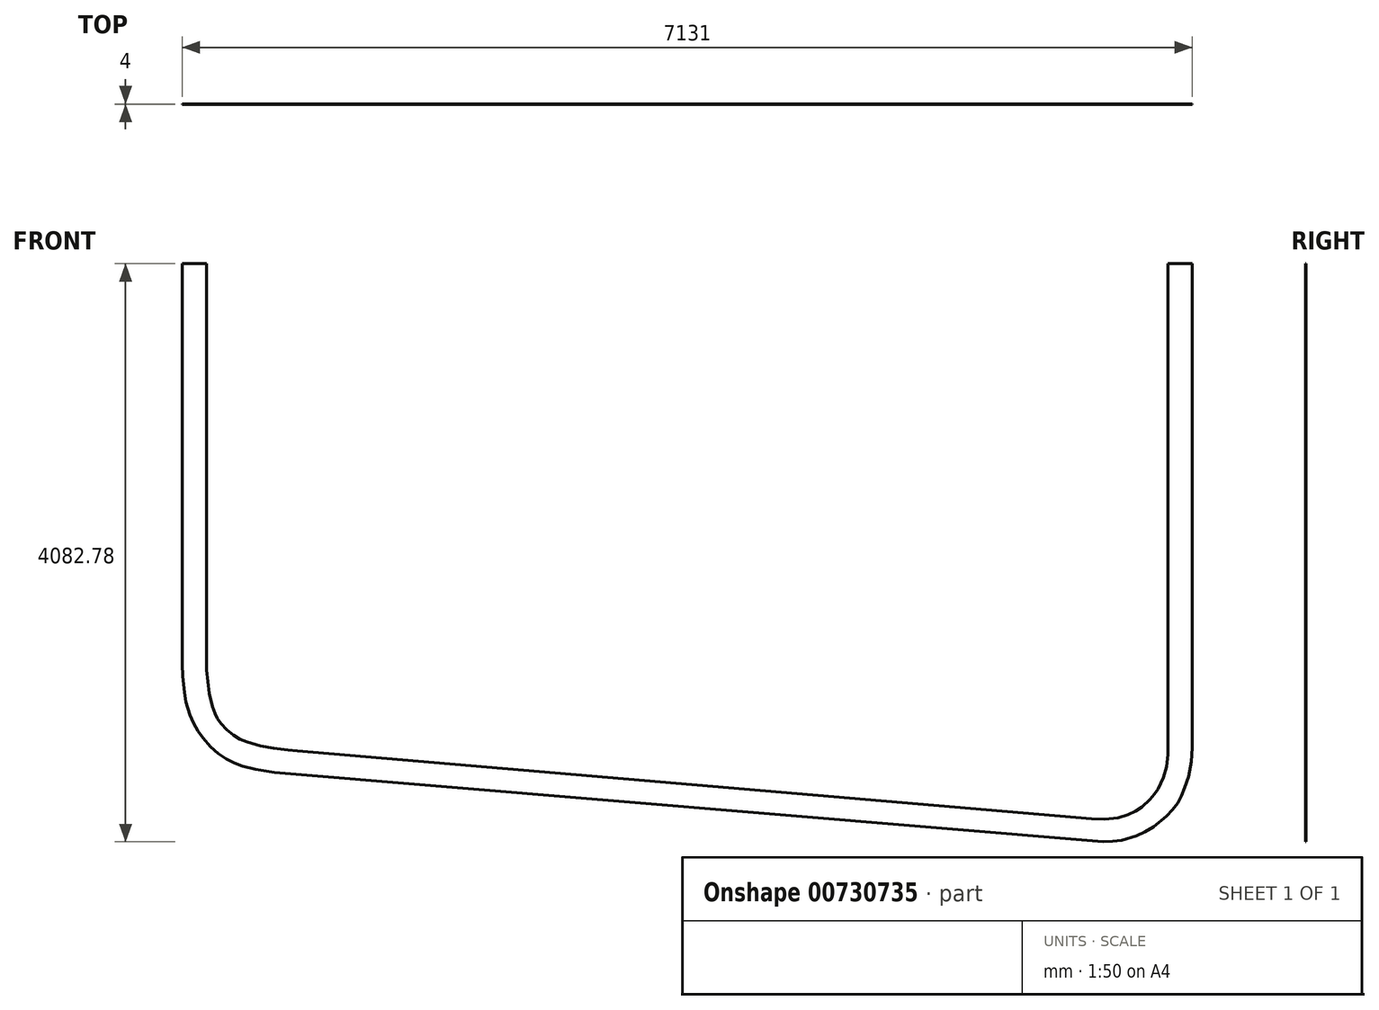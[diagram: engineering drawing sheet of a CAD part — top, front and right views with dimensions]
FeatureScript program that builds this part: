
annotation { "Feature Type Name" : "Feature", "Feature Type Description" : "" }
export const myFeature = defineFeature(function(context is Context, id is Id, definition is map)
    precondition{}
    {
        {
            var Q0;
            Q0=qCreatedBy(makeId("Front.planeOp"),FACE);
            var sketch = newSketch(context, id + "F0", { "sketchPlane" : qUnion([Q0])});
            skLineSegment(sketch, "E0", {"start": v(-3565.5, 2041.39) * mm, "end": v(-3393, 2041.39) * mm});
            skLineSegment(sketch, "E1", {"start": v(-3393, 2041.39) * mm, "end": v(-3393, -828.13) * mm});
            skLineSegment(sketch, "E2", {"start": v(-3393, -828.13) * mm, "end": v(-3520, -828.13) * mm});
            skLineSegment(sketch, "E3", {"start": v(-3520, -828.13) * mm, "end": v(-3393, -828.13) * mm});
            skLineSegment(sketch, "E4", {"start": v(-3393, -828.13) * mm, "end": v(-3386.3, -909.28) * mm});
            skLineSegment(sketch, "E5", {"start": v(-3386.3, -909.28) * mm, "end": v(-3373.83, -991.93) * mm});
            skLineSegment(sketch, "E6", {"start": v(-3373.83, -991.93) * mm, "end": v(-3351.53, -1085.79) * mm});
            skLineSegment(sketch, "E7", {"start": v(-3351.53, -1085.79) * mm, "end": v(-3335.35, -1135.42) * mm});
            skLineSegment(sketch, "E8", {"start": v(-3335.35, -1135.42) * mm, "end": v(-3316.9, -1172) * mm});
            skLineSegment(sketch, "E9", {"start": v(-3316.9, -1172) * mm, "end": v(-3293.52, -1205.83) * mm});
            skLineSegment(sketch, "E10", {"start": v(-3293.52, -1205.83) * mm, "end": v(-3252.06, -1250.38) * mm});
            skLineSegment(sketch, "E11", {"start": v(-3252.06, -1250.38) * mm, "end": v(-3204.21, -1288.07) * mm});
            skLineSegment(sketch, "E12", {"start": v(-3204.21, -1288.07) * mm, "end": v(-3158.57, -1315.07) * mm});
            skLineSegment(sketch, "E13", {"start": v(-3158.57, -1315.07) * mm, "end": v(-3110.1, -1336.3) * mm});
            skLineSegment(sketch, "E14", {"start": v(-3110.1, -1336.3) * mm, "end": v(-3012.31, -1363.2) * mm});
            skLineSegment(sketch, "E15", {"start": v(-3012.31, -1363.2) * mm, "end": v(-2920.67, -1380.73) * mm});
            skLineSegment(sketch, "E16", {"start": v(-2920.67, -1380.73) * mm, "end": v(-2819.12, -1392.54) * mm});
            skLineSegment(sketch, "E17", {"start": v(-2819.12, -1392.54) * mm, "end": v(-2753.87, -1400.7) * mm});
            skLineSegment(sketch, "E18", {"start": v(-2753.87, -1400.7) * mm, "end": v(-2769.64, -1526.7) * mm});
            skLineSegment(sketch, "E19", {"start": v(-2769.64, -1526.7) * mm, "end": v(-2753.87, -1400.7) * mm});
            skLineSegment(sketch, "E20", {"start": v(-2753.87, -1400.7) * mm, "end": v(2854.12, -1880.1) * mm});
            skLineSegment(sketch, "E21", {"start": v(2854.12, -1880.1) * mm, "end": v(2843.33, -2006.64) * mm});
            skLineSegment(sketch, "E22", {"start": v(2843.33, -2006.64) * mm, "end": v(2854.12, -1880.1) * mm});
            skLineSegment(sketch, "E23", {"start": v(2854.12, -1880.1) * mm, "end": v(2944.95, -1882.43) * mm});
            skLineSegment(sketch, "E24", {"start": v(2944.95, -1882.43) * mm, "end": v(3041.5, -1871.66) * mm});
            skLineSegment(sketch, "E25", {"start": v(3041.5, -1871.66) * mm, "end": v(3111.83, -1848.42) * mm});
            skLineSegment(sketch, "E26", {"start": v(3111.83, -1848.42) * mm, "end": v(3164.79, -1825.54) * mm});
            skLineSegment(sketch, "E27", {"start": v(3164.79, -1825.54) * mm, "end": v(3209.44, -1797.04) * mm});
            skLineSegment(sketch, "E28", {"start": v(3209.44, -1797.04) * mm, "end": v(3267.35, -1742.66) * mm});
            skLineSegment(sketch, "E29", {"start": v(3267.35, -1742.66) * mm, "end": v(3298.83, -1704.86) * mm});
            skLineSegment(sketch, "E30", {"start": v(3298.83, -1704.86) * mm, "end": v(3322.68, -1669.28) * mm});
            skLineSegment(sketch, "E31", {"start": v(3322.68, -1669.28) * mm, "end": v(3361.51, -1586.37) * mm});
            skLineSegment(sketch, "E32", {"start": v(3361.51, -1586.37) * mm, "end": v(3384.98, -1511.19) * mm});
            skLineSegment(sketch, "E33", {"start": v(3384.98, -1511.19) * mm, "end": v(3393.06, -1425.28) * mm});
            skLineSegment(sketch, "E34", {"start": v(3393.06, -1425.28) * mm, "end": v(3519.5, -1437.14) * mm});
            skLineSegment(sketch, "E35", {"start": v(3519.5, -1437.14) * mm, "end": v(3393.06, -1425.28) * mm});
            skLineSegment(sketch, "E36", {"start": v(3393.06, -1425.28) * mm, "end": v(3393.06, 2041.39) * mm});
            skLineSegment(sketch, "E37", {"start": v(3393.06, 2041.39) * mm, "end": v(3565.5, 2041.39) * mm});
            skLineSegment(sketch, "E38", {"start": v(3565.5, 2041.39) * mm, "end": v(3565.5, -1377.81) * mm});
            skLineSegment(sketch, "E39", {"start": v(3565.5, -1377.81) * mm, "end": v(3438.5, -1377.81) * mm});
            skLineSegment(sketch, "E40", {"start": v(3438.5, -1377.81) * mm, "end": v(3565.5, -1377.81) * mm});
            skLineSegment(sketch, "E41", {"start": v(3565.5, -1377.81) * mm, "end": v(3557.52, -1474.46) * mm});
            skLineSegment(sketch, "E42", {"start": v(3557.52, -1474.46) * mm, "end": v(3539.03, -1579.56) * mm});
            skLineSegment(sketch, "E43", {"start": v(3539.03, -1579.56) * mm, "end": v(3512.57, -1659.7) * mm});
            skLineSegment(sketch, "E44", {"start": v(3512.57, -1659.7) * mm, "end": v(3490.37, -1715.3) * mm});
            skLineSegment(sketch, "E45", {"start": v(3490.37, -1715.3) * mm, "end": v(3462.76, -1767.9) * mm});
            skLineSegment(sketch, "E46", {"start": v(3462.76, -1767.9) * mm, "end": v(3426.59, -1815.6) * mm});
            skLineSegment(sketch, "E47", {"start": v(3426.59, -1815.6) * mm, "end": v(3384.58, -1858.91) * mm});
            skLineSegment(sketch, "E48", {"start": v(3384.58, -1858.91) * mm, "end": v(3291.13, -1936.03) * mm});
            skLineSegment(sketch, "E49", {"start": v(3291.13, -1936.03) * mm, "end": v(3233.6, -1970.87) * mm});
            skLineSegment(sketch, "E50", {"start": v(3233.6, -1970.87) * mm, "end": v(3172.43, -1999.02) * mm});
            skLineSegment(sketch, "E51", {"start": v(3172.43, -1999.02) * mm, "end": v(3068.02, -2029.5) * mm});
            skLineSegment(sketch, "E52", {"start": v(3068.02, -2029.5) * mm, "end": v(3002.74, -2038.85) * mm});
            skLineSegment(sketch, "E53", {"start": v(3002.74, -2038.85) * mm, "end": v(2936.88, -2041.39) * mm});
            skLineSegment(sketch, "E54", {"start": v(2936.88, -2041.39) * mm, "end": v(2932, -1914.49) * mm});
            skLineSegment(sketch, "E55", {"start": v(2932, -1914.49) * mm, "end": v(2936.88, -2041.39) * mm});
            skLineSegment(sketch, "E56", {"start": v(2936.88, -2041.39) * mm, "end": v(-2915, -1550.6) * mm});
            skLineSegment(sketch, "E57", {"start": v(-2915, -1550.6) * mm, "end": v(-2904.39, -1424.04) * mm});
            skLineSegment(sketch, "E58", {"start": v(-2904.39, -1424.04) * mm, "end": v(-2915, -1550.6) * mm});
            skLineSegment(sketch, "E59", {"start": v(-2915, -1550.6) * mm, "end": v(-3047.26, -1528.38) * mm});
            skLineSegment(sketch, "E60", {"start": v(-3047.26, -1528.38) * mm, "end": v(-3139.97, -1506.51) * mm});
            skLineSegment(sketch, "E61", {"start": v(-3139.97, -1506.51) * mm, "end": v(-3198.06, -1483.73) * mm});
            skLineSegment(sketch, "E62", {"start": v(-3198.06, -1483.73) * mm, "end": v(-3253.51, -1454.75) * mm});
            skLineSegment(sketch, "E63", {"start": v(-3253.51, -1454.75) * mm, "end": v(-3312.6, -1416.7) * mm});
            skLineSegment(sketch, "E64", {"start": v(-3312.6, -1416.7) * mm, "end": v(-3367.02, -1371.13) * mm});
            skLineSegment(sketch, "E65", {"start": v(-3367.02, -1371.13) * mm, "end": v(-3420.34, -1308.19) * mm});
            skLineSegment(sketch, "E66", {"start": v(-3420.34, -1308.19) * mm, "end": v(-3455.19, -1258.81) * mm});
            skLineSegment(sketch, "E67", {"start": v(-3455.19, -1258.81) * mm, "end": v(-3485.85, -1202.12) * mm});
            skLineSegment(sketch, "E68", {"start": v(-3485.85, -1202.12) * mm, "end": v(-3510.48, -1144.3) * mm});
            skLineSegment(sketch, "E69", {"start": v(-3510.48, -1144.3) * mm, "end": v(-3539.08, -1053.9) * mm});
            skLineSegment(sketch, "E70", {"start": v(-3539.08, -1053.9) * mm, "end": v(-3550.7, -986.7) * mm});
            skLineSegment(sketch, "E71", {"start": v(-3550.7, -986.7) * mm, "end": v(-3562.4, -873.26) * mm});
            skLineSegment(sketch, "E72", {"start": v(-3562.4, -873.26) * mm, "end": v(-3565.5, -784.95) * mm});
            skLineSegment(sketch, "E73", {"start": v(-3565.5, -784.95) * mm, "end": v(-3438.58, -780.48) * mm});
            skLineSegment(sketch, "E74", {"start": v(-3438.58, -780.48) * mm, "end": v(-3565.5, -784.95) * mm});
            skLineSegment(sketch, "E75", {"start": v(-3565.5, -784.95) * mm, "end": v(-3565.5, 2041.39) * mm});
            skSolve(sketch);
        }
        {
            var Q0;
            Q0 = qSketchRegion(id + "F0", true);
            extrude(context, id + "F1", {"entities" : qUnion([Q0]), "depth" : 4 * mm, "offsetDistance" : 25 * mm});
        }
    });
